# Revit family: ВКПІ Л М
name_source: partatom
category: Mechanical Equipment
units: mm (PartAtom-declared; Revit-internal decimal feet)

## family parameters
Always vertical = Yes
Classification = None
Cut with Voids When Loaded = No
Part Type = Normal
Room Calculation Point = No
Round Connector Dimension = Use Diameter
Shared = No
Work Plane-Based = No

## types (16) — shared parameters
00_20_Виробник = Вентс
00_20_Назва = Відцентровий вентилятор
Description = Для прямокутних каналів
Manufacturer = Вентс
URL = https://vents.ua
w = 50 mm  [stored 0.164042 ft]
Класифікація навантаження = HVAC
Матеріал зони обслуговуваня = <By Category>
Матеріал корпусу = Сталь, гальванізована
Температура повітря, що переміщається = -25...+50 °C
Частота = 50 Hz
zero-valued in all types: Default Elevation

## per-type parameters (varying)
- ВКПІ 300х150 М1 ЕС: 00_20_Тип=ВКПІ 300х150 М1 ЕС; 2 Ручка=No; B=300 mm; B1=320 mm; B2=340 mm; B3=364 mm; Be=129 mm; F=364 mm; H=150 mm; H1=170 mm  [stored 0.557743 ft]; H2=190 mm  [stored 0.62336 ft]; H3=271 mm  [stored 0.889108 ft]; He=250 mm  [stored 0.82021 ft]; K=50 mm  [stored 0.164042 ft]; L=370 mm; Le=19 mm; a=40 mm  [stored 0.131234 ft]; b3=91 mm  [stored 0.298556 ft]; h=41 mm  [stored 0.134514 ft]; h1=271 mm  [stored 0.889108 ft]; k=123 mm; l=120 mm  [stored 0.393701 ft]; l1=70 mm  [stored 0.229659 ft]; Вага=10.30 kg; Висота=271 mm  [stored 0.889108 ft]; Довжина=370 mm; Клемная коробка=Yes; Кронштейн=No; Кількість фаз=1; Максимальний потік повітря=565.0 m³/h; Напруга=230 V; Потужність=97 W; Рівень звукового тиску на відстані 3 м=29 дБА; Струм=1 A; Установлена потужність=168 VA; Ширина=364 mm; Штуцер=No
- ВКПІ 1000х500 Л3 ЕС: 00_20_Тип=ВКПІ 300х150 М1 ЕС; 2 Ручка=Yes; B=1000 mm; B1=1020 mm; B2=1040 mm; B3=1064 mm; Be=532 mm; F=1183 mm; H=500 mm; H1=520 mm; H2=540 mm; H3=814 mm; He=546 mm; K=850 mm; L=1052 mm; Le=263 mm  [stored 0.862861 ft]; a=60 mm  [stored 0.19685 ft]; b3=266 mm  [stored 0.872703 ft]; h=46 mm; h1=550 mm; k=425 mm; l=470 mm; l1=420 mm; Вага=130.00 kg; Висота=814 mm; Довжина=1052 mm; Клемная коробка=No; Кронштейн=Yes; Кількість фаз=3; Максимальний потік повітря=11190.0 m³/h; Напруга=400 V; Потужність=3429 W; Рівень звукового тиску на відстані 3 м=47 дБА; Струм=5 A; Установлена потужність=2000 VA; Ширина=1064 mm; Штуцер=Yes
- ВКПІ 300х150 Л1 ЕС: 00_20_Тип=ВКПІ 300х150 Л1 ЕС; 2 Ручка=No; B=300 mm; B1=320 mm; B2=340 mm; B3=364 mm; Be=129 mm; F=364 mm; H=150 mm; H1=170 mm  [stored 0.557743 ft]; H2=190 mm  [stored 0.62336 ft]; H3=271 mm  [stored 0.889108 ft]; He=250 mm  [stored 0.82021 ft]; K=50 mm  [stored 0.164042 ft]; L=370 mm; Le=19 mm; a=40 mm  [stored 0.131234 ft]; b3=91 mm  [stored 0.298556 ft]; h=41 mm  [stored 0.134514 ft]; h1=271 mm  [stored 0.889108 ft]; k=123 mm; l=120 mm  [stored 0.393701 ft]; l1=70 mm  [stored 0.229659 ft]; Вага=10.30 kg; Висота=271 mm  [stored 0.889108 ft]; Довжина=370 mm; Клемная коробка=Yes; Кронштейн=No; Кількість фаз=1; Максимальний потік повітря=665.0 m³/h; Напруга=230 V; Потужність=101 W; Рівень звукового тиску на відстані 3 м=30 дБА; Струм=1 A; Установлена потужність=184 VA; Ширина=364 mm; Штуцер=No
- ВКПІ 400х200 М1 ЕС: 00_20_Тип=ВКПІ 400х200 М1 ЕС; 2 Ручка=No; B=400 mm; B1=420 mm; B2=440 mm; B3=464 mm; Be=154 mm; F=464 mm; H=200 mm  [stored 0.656168 ft]; H1=220 mm  [stored 0.721785 ft]; H2=240 mm  [stored 0.787402 ft]; H3=322 mm; He=301 mm; K=50 mm  [stored 0.164042 ft]; L=460 mm; Le=19 mm; a=40 mm  [stored 0.131234 ft]; b3=116 mm  [stored 0.380577 ft]; h=41 mm  [stored 0.134514 ft]; h1=322 mm; k=153 mm; l=170 mm  [stored 0.557743 ft]; l1=120 mm  [stored 0.393701 ft]; Вага=15.10 kg; Висота=322 mm; Довжина=460 mm; Клемная коробка=Yes; Кронштейн=No; Кількість фаз=1; Максимальний потік повітря=810.0 m³/h; Напруга=230 V; Потужність=91 W; Рівень звукового тиску на відстані 3 м=33 дБА; Струм=1 A; Установлена потужність=159 VA; Ширина=464 mm; Штуцер=No
- ВКПІ 400х200 Л1 ЕС: 00_20_Тип=ВКПІ 400х200 Л1 ЕС; 2 Ручка=No; B=400 mm; B1=420 mm; B2=440 mm; B3=464 mm; Be=154 mm; F=464 mm; H=200 mm  [stored 0.656168 ft]; H1=220 mm  [stored 0.721785 ft]; H2=240 mm  [stored 0.787402 ft]; H3=322 mm; He=301 mm; K=50 mm  [stored 0.164042 ft]; L=460 mm; Le=19 mm; a=40 mm  [stored 0.131234 ft]; b3=116 mm  [stored 0.380577 ft]; h=41 mm  [stored 0.134514 ft]; h1=322 mm; k=153 mm; l=170 mm  [stored 0.557743 ft]; l1=120 mm  [stored 0.393701 ft]; Вага=16.80 kg; Висота=322 mm; Довжина=460 mm; Клемная коробка=Yes; Кронштейн=No; Кількість фаз=1; Максимальний потік повітря=1190.0 m³/h; Напруга=230 V; Потужність=192 W; Рівень звукового тиску на відстані 3 м=30 дБА; Струм=1 A; Установлена потужність=329 VA; Ширина=464 mm; Штуцер=No
- ВКПІ 500х250 М1 ЕС: 00_20_Тип=ВКПІ 500х250 М1 ЕС; 2 Ручка=No; B=500 mm; B1=520 mm; B2=540 mm; B3=564 mm; Be=179 mm; F=564 mm; H=250 mm  [stored 0.82021 ft]; H1=270 mm  [stored 0.885827 ft]; H2=290 mm  [stored 0.951444 ft]; H3=373 mm; He=352 mm; K=50 mm  [stored 0.164042 ft]; L=560 mm; Le=19 mm; a=40 mm  [stored 0.131234 ft]; b3=141 mm; h=42 mm  [stored 0.137795 ft]; h1=373 mm; k=187 mm; l=220 mm  [stored 0.721785 ft]; l1=170 mm  [stored 0.557743 ft]; Вага=25.50 kg; Висота=373 mm; Довжина=560 mm; Клемная коробка=Yes; Кронштейн=No; Кількість фаз=1; Максимальний потік повітря=1590.0 m³/h; Напруга=230 V; Потужність=252 W; Рівень звукового тиску на відстані 3 м=34 дБА; Струм=2 A; Установлена потужність=426 VA; Ширина=564 mm; Штуцер=No
- ВКПІ 500х250 Л1 ЕС: 00_20_Тип=ВКПІ 500х250 Л1 ЕС; 2 Ручка=No; B=500 mm; B1=520 mm; B2=540 mm; B3=564 mm; Be=179 mm; F=564 mm; H=250 mm  [stored 0.82021 ft]; H1=270 mm  [stored 0.885827 ft]; H2=290 mm  [stored 0.951444 ft]; H3=373 mm; He=352 mm; K=50 mm  [stored 0.164042 ft]; L=560 mm; Le=19 mm; a=40 mm  [stored 0.131234 ft]; b3=141 mm; h=42 mm  [stored 0.137795 ft]; h1=373 mm; k=187 mm; l=220 mm  [stored 0.721785 ft]; l1=170 mm  [stored 0.557743 ft]; Вага=27.70 kg; Висота=373 mm; Довжина=560 mm; Клемная коробка=Yes; Кронштейн=No; Кількість фаз=1; Максимальний потік повітря=2480.0 m³/h; Напруга=230 V; Потужність=555 W; Рівень звукового тиску на відстані 3 м=51 дБА; Струм=4 A; Установлена потужність=943 VA; Ширина=564 mm; Штуцер=No
- ВКПІ 500х300 Л1 ЕС: 00_20_Тип=ВКПІ 500х300 Л1 ЕС; 2 Ручка=No; B=500 mm; B1=520 mm; B2=540 mm; B3=564 mm; Be=179 mm; F=564 mm; H=300 mm; H1=320 mm; H2=340 mm; H3=424 mm; He=403 mm; K=50 mm  [stored 0.164042 ft]; L=560 mm; Le=19 mm; a=40 mm  [stored 0.131234 ft]; b3=141 mm; h=42 mm  [stored 0.137795 ft]; h1=424 mm; k=187 mm; l=220 mm  [stored 0.721785 ft]; l1=170 mm  [stored 0.557743 ft]; Вага=29.00 kg; Висота=424 mm; Довжина=560 mm; Клемная коробка=Yes; Кронштейн=No; Кількість фаз=1; Максимальний потік повітря=3230.0 m³/h; Напруга=230 V; Потужність=445 W; Рівень звукового тиску на відстані 3 м=43 дБА; Струм=3 A; Установлена потужність=766 VA; Ширина=564 mm; Штуцер=No
- ВКПІ 600х300 М1 ЕС: 00_20_Тип=ВКПІ 600х300 М1 ЕС; 2 Ручка=Yes; B=600 mm; B1=620 mm; B2=640 mm; B3=664 mm; Be=332 mm; F=783 mm; H=300 mm; H1=320 mm; H2=340 mm; H3=574 mm; He=339 mm; K=450 mm; L=752 mm; Le=188 mm  [stored 0.616798 ft]; a=60 mm  [stored 0.19685 ft]; b3=166 mm  [stored 0.544619 ft]; h=39 mm  [stored 0.127953 ft]; h1=350 mm; k=225 mm  [stored 0.738189 ft]; l=270 mm  [stored 0.885827 ft]; l1=220 mm  [stored 0.721785 ft]; Вага=52.90 kg; Висота=574 mm; Довжина=752 mm; Клемная коробка=No; Кронштейн=Yes; Кількість фаз=1; Максимальний потік повітря=2545.0 m³/h; Напруга=230 V; Потужність=326 W; Рівень звукового тиску на відстані 3 м=34 дБА; Струм=2 A; Установлена потужність=564 VA; Ширина=664 mm; Штуцер=Yes
- ВКПІ 600х350 М1 ЕС: 00_20_Тип=ВКПІ 600х350 М1 ЕС; 2 Ручка=Yes; B=600 mm; B1=620 mm; B2=640 mm; B3=664 mm; Be=332 mm; F=783 mm; H=350 mm; H1=370 mm; H2=390 mm; H3=664 mm; He=396 mm; K=450 mm; L=752 mm; Le=188 mm  [stored 0.616798 ft]; a=60 mm  [stored 0.19685 ft]; b3=166 mm  [stored 0.544619 ft]; h=46 mm; h1=400 mm; k=225 mm  [stored 0.738189 ft]; l=270 mm  [stored 0.885827 ft]; l1=220 mm  [stored 0.721785 ft]; Вага=56.60 kg; Висота=664 mm; Довжина=752 mm; Клемная коробка=No; Кронштейн=Yes; Кількість фаз=1; Максимальний потік повітря=2815.0 m³/h; Напруга=230 V; Потужність=361 W; Рівень звукового тиску на відстані 3 м=38 дБА; Струм=3 A; Установлена потужність=603 VA; Ширина=664 mm; Штуцер=Yes
- ВКПІ 600х350 Л3 ЕС: 00_20_Тип=ВКПІ 600х350 Л3 ЕС; 2 Ручка=Yes; B=600 mm; B1=620 mm; B2=640 mm; B3=664 mm; Be=332 mm; F=783 mm; H=350 mm; H1=370 mm; H2=390 mm; H3=664 mm; He=396 mm; K=450 mm; L=752 mm; Le=188 mm  [stored 0.616798 ft]; a=60 mm  [stored 0.19685 ft]; b3=166 mm  [stored 0.544619 ft]; h=46 mm; h1=400 mm; k=225 mm  [stored 0.738189 ft]; l=270 mm  [stored 0.885827 ft]; l1=220 mm  [stored 0.721785 ft]; Вага=59.30 kg; Висота=664 mm; Довжина=752 mm; Клемная коробка=No; Кронштейн=Yes; Кількість фаз=3; Максимальний потік повітря=4290.0 m³/h; Напруга=400 V; Потужність=1308 W; Рівень звукового тиску на відстані 3 м=40 дБА; Струм=2 A; Установлена потужність=940 VA; Ширина=664 mm; Штуцер=Yes
- ВКПІ 700х400 М1 ЕС: 00_20_Тип=ВКПІ 700х400 М1 ЕС; 2 Ручка=Yes; B=700 mm; B1=720 mm; B2=740 mm; B3=764 mm; Be=382 mm; F=883 mm; H=400 mm; H1=420 mm; H2=440 mm; H3=714 mm; He=446 mm; K=742 mm; L=882 mm; Le=221 mm; a=60 mm  [stored 0.19685 ft]; b3=191 mm  [stored 0.62664 ft]; h=46 mm; h1=450 mm; k=371 mm; l=320 mm; l1=270 mm  [stored 0.885827 ft]; Вага=82.60 kg; Висота=714 mm; Довжина=882 mm; Клемная коробка=No; Кронштейн=Yes; Кількість фаз=1; Максимальний потік повітря=5710.0 m³/h; Напруга=230 V; Потужність=795 W; Рівень звукового тиску на відстані 3 м=37 дБА; Струм=3 A; Установлена потужність=800 VA; Ширина=764 mm; Штуцер=Yes
- ВКПІ 700х400 Л3 ЕС: 00_20_Тип=ВКПІ 700х400 Л3 ЕС; 2 Ручка=Yes; B=700 mm; B1=720 mm; B2=740 mm; B3=764 mm; Be=382 mm; F=883 mm; H=400 mm; H1=420 mm; H2=440 mm; H3=714 mm; He=446 mm; K=742 mm; L=882 mm; Le=221 mm; a=60 mm  [stored 0.19685 ft]; b3=191 mm  [stored 0.62664 ft]; h=46 mm; h1=450 mm; k=371 mm; l=320 mm; l1=270 mm  [stored 0.885827 ft]; Вага=83.40 kg; Висота=714 mm; Довжина=882 mm; Клемная коробка=No; Кронштейн=Yes; Кількість фаз=3; Максимальний потік повітря=6810.0 m³/h; Напруга=400 V; Потужність=2748 W; Рівень звукового тиску на відстані 3 м=43 дБА; Струм=3 A; Установлена потужність=1120 VA; Ширина=764 mm; Штуцер=Yes
- ВКПІ 800х500 М3 ЕС: 00_20_Тип=ВКПІ 800х500 М3 ЕС; 2 Ручка=Yes; B=800 mm; B1=820 mm; B2=840 mm; B3=864 mm; Be=432 mm; F=983 mm; H=500 mm; H1=520 mm; H2=540 mm; H3=814 mm; He=546 mm; K=797 mm; L=937 mm; Le=234 mm; a=60 mm  [stored 0.19685 ft]; b3=216 mm  [stored 0.708661 ft]; h=46 mm; h1=550 mm; k=399 mm; l=370 mm; l1=320 mm; Вага=108.40 kg; Висота=814 mm; Довжина=937 mm; Клемная коробка=No; Кронштейн=Yes; Кількість фаз=3; Максимальний потік повітря=8395.0 m³/h; Напруга=400 V; Потужність=2025 W; Рівень звукового тиску на відстані 3 м=43 дБА; Струм=2 A; Установлена потужність=804 VA; Ширина=864 mm; Штуцер=Yes
- ВКПІ 800х500 Л3 ЕС: 00_20_Тип=ВКПІ 800х500 Л3 ЕС; 2 Ручка=Yes; B=800 mm; B1=820 mm; B2=840 mm; B3=864 mm; Be=432 mm; F=983 mm; H=500 mm; H1=520 mm; H2=540 mm; H3=814 mm; He=546 mm; K=797 mm; L=937 mm; Le=234 mm; a=60 mm  [stored 0.19685 ft]; b3=216 mm  [stored 0.708661 ft]; h=46 mm; h1=550 mm; k=399 mm; l=370 mm; l1=320 mm; Вага=99.80 kg; Висота=814 mm; Довжина=937 mm; Клемная коробка=No; Кронштейн=Yes; Кількість фаз=3; Максимальний потік повітря=8535.0 m³/h; Напруга=400 V; Потужність=2925 W; Рівень звукового тиску на відстані 3 м=42 дБА; Струм=3 A; Установлена потужність=1220 VA; Ширина=864 mm; Штуцер=Yes
- ВКПІ 900х500 Л3 ЕС: 00_20_Тип=ВКПІ 900х500 Л3 ЕС; 2 Ручка=Yes; B=900 mm; B1=920 mm; B2=940 mm; B3=964 mm; Be=482 mm; F=1083 mm; H=500 mm; H1=520 mm; H2=540 mm; H3=814 mm; He=546 mm; K=850 mm; L=1052 mm; Le=263 mm  [stored 0.862861 ft]; a=60 mm  [stored 0.19685 ft]; b3=241 mm  [stored 0.790682 ft]; h=46 mm; h1=550 mm; k=425 mm; l=420 mm; l1=370 mm; Вага=120.00 kg; Висота=814 mm; Довжина=1052 mm; Клемная коробка=No; Кронштейн=Yes; Кількість фаз=3; Максимальний потік повітря=11190.0 m³/h; Напруга=400 V; Потужність=3429 W; Рівень звукового тиску на відстані 3 м=47 дБА; Струм=5 A; Установлена потужність=2000 VA; Ширина=964 mm; Штуцер=Yes

note: [stored X ft] marks values corroborated as IEEE doubles in the binary element streams (Revit-internal decimal feet)
